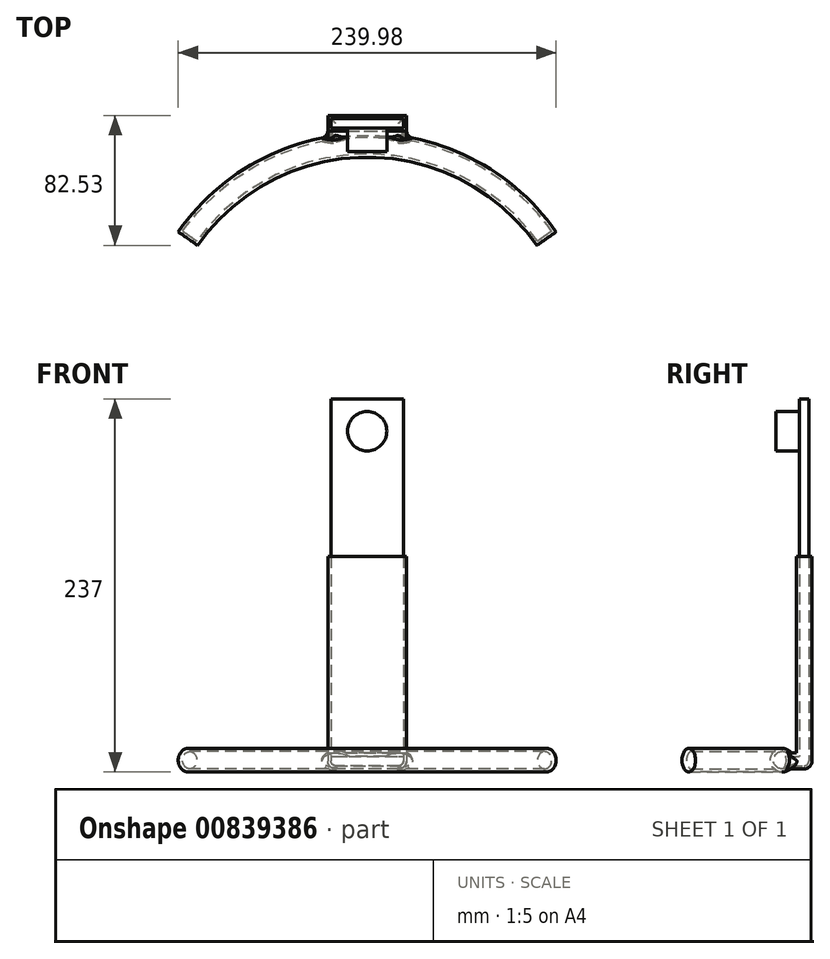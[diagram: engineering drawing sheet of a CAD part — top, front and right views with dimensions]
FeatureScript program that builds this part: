
annotation { "Feature Type Name" : "Feature", "Feature Type Description" : "" }
export const myFeature = defineFeature(function(context is Context, id is Id, definition is map)
    precondition{}
    {
        {
            var Q0;
            Q0=qCreatedBy(makeId("Right.planeOp"),FACE);
            var sketch = newSketch(context, id + "F0", { "sketchPlane" : qUnion([Q0])});
            skLineSegment(sketch, "E0", {"start": v(-100.7, 15.32) * mm, "end": v(-100.7, -57.91) * mm});
            skCircle(sketch, "E1", {"center": v(38.3, 0) * mm, "radius": 7.5 * mm});
            skSolve(sketch);
        }
        {
            var Q0;
            Q0=makeQuery(id+"F0.imprint","IMPRINT",FACE,{"disambiguationData":[TD([[makeQuery(id+"F0.imprint","IMPRINT",EDGE,{"derivedFrom":sQuery(id+"F0.wireOp",EDGE,"E1")}),1.0]])]});
            var Q1;
            Q1=sQuery(id+"F0.wireOp",EDGE,"E0");
            revolve(context, id + "F1", {"surfaceOperationType" : NewSurfaceOperationType.NEW, "entities" : qUnion([Q0]), "axis" : qUnion([Q1]), "revolveType" : RevolveType.SYMMETRIC, "angle" : 110 * degree});
        }
        {
            var Q0;
            Q0=qCreatedBy(makeId("Right.planeOp"),FACE);
            var sketch = newSketch(context, id + "F2", { "sketchPlane" : qUnion([Q0])});
            skLineSegment(sketch, "E2.bottom", {"start": v(37.26, 4.5) * mm, "end": v(57.26, 4.5) * mm});
            skLineSegment(sketch, "E2.top", {"start": v(37.26, -5.5) * mm, "end": v(57.26, -5.5) * mm});
            skLineSegment(sketch, "E2.left", {"start": v(37.26, 4.5) * mm, "end": v(37.26, -5.5) * mm});
            skLineSegment(sketch, "E2.right", {"start": v(57.26, 4.5) * mm, "end": v(57.26, -5.5) * mm});
            skSolve(sketch);
        }
        {
            var Q0;
            Q0=makeQuery(id+"F2.imprint","IMPRINT",FACE,{"disambiguationData":[TD([[makeQuery(id+"F2.imprint","IMPRINT",EDGE,{"derivedFrom":sQuery(id+"F2.wireOp",EDGE,"E2.bottom")}),-1.0]])]});
            extrude(context, id + "F3", {"entities" : qUnion([Q0]), "operationType" : NewBodyOperationType.ADD, "depth" : 25 * mm, "offsetDistance" : 25 * mm, "hasSecondDirection" : true, "secondDirectionOppositeDirection" : true, "secondDirectionDepth" : 25 * mm});
        }
        {
            var Q0;
            Q0=makeQuery(id+"F3.opExtrude","SWEPT_FACE",FACE,{"disambiguationData":[OSD([sQuery(id+"F2.wireOp",EDGE,"E2.bottom")])]});
            var sketch = newSketch(context, id + "F4", { "sketchPlane" : qUnion([Q0])});
            skLineSegment(sketch, "E3.bottom", {"start": v(-25, 47.26) * mm, "end": v(25, 47.26) * mm});
            skLineSegment(sketch, "E3.top", {"start": v(-25, 57.26) * mm, "end": v(25, 57.26) * mm});
            skLineSegment(sketch, "E3.left", {"start": v(-25, 47.26) * mm, "end": v(-25, 57.26) * mm});
            skLineSegment(sketch, "E3.right", {"start": v(25, 47.26) * mm, "end": v(25, 57.26) * mm});
            skSolve(sketch);
        }
        {
            var Q0;
            Q0=makeQuery(id+"F4.imprint","IMPRINT",FACE,{"disambiguationData":[TD([[makeQuery(id+"F4.imprint","IMPRINT",EDGE,{"derivedFrom":sQuery(id+"F4.wireOp",EDGE,"E3.bottom")}),1.0]])]});
            extrude(context, id + "F5", {"entities" : qUnion([Q0]), "operationType" : NewBodyOperationType.ADD, "depth" : 125 * mm, "offsetDistance" : 25 * mm});
        }
        {
            var Q0;
            Q0=makeQuery(id+"F3.opExtrude","SWEPT_FACE",FACE,{"disambiguationData":[OSD([sQuery(id+"F2.wireOp",EDGE,"E2.top")])]});
            fillet(context, id + "F6", {"entities" : qUnion([Q0]), "radius" : 5 * mm, "tangentPropagation" : true, "allowEdgeOverflow" : false});
        }
        {
            var Q0;
            Q0=makeQuery(id+"F5.opExtrude","CAP_FACE",FACE,{"disambiguationData":[OSD([sQuery(id+"F4.wireOp",EDGE,"E3.bottom"),sQuery(id+"F4.wireOp",EDGE,"E3.top"),sQuery(id+"F4.wireOp",EDGE,"E3.left"),sQuery(id+"F4.wireOp",EDGE,"E3.right")])],"isStart":false});
            shell(context, id + "F7", {"entities" : qUnion([Q0]), "thickness" : 2 * mm});
        }
        {
            var Q0;
            Q0=makeQuery(id+"F5.opExtrude","CAP_FACE",FACE,{"disambiguationData":[OSD([sQuery(id+"F4.wireOp",EDGE,"E3.bottom"),sQuery(id+"F4.wireOp",EDGE,"E3.top"),sQuery(id+"F4.wireOp",EDGE,"E3.left"),sQuery(id+"F4.wireOp",EDGE,"E3.right")])],"isStart":false});
            var sketch = newSketch(context, id + "F8", { "sketchPlane" : qUnion([Q0])});
            skLineSegment(sketch, "E4.bottom", {"start": v(-23, 49.26) * mm, "end": v(23, 49.26) * mm});
            skLineSegment(sketch, "E4.top", {"start": v(-23, 55.26) * mm, "end": v(23, 55.26) * mm});
            skLineSegment(sketch, "E4.left", {"start": v(-23, 49.26) * mm, "end": v(-23, 55.26) * mm});
            skLineSegment(sketch, "E4.right", {"start": v(23, 49.26) * mm, "end": v(23, 55.26) * mm});
            skSolve(sketch);
        }
        {
            var Q0;
            Q0 = qSketchRegion(id + "F8", true);
            extrude(context, id + "F9", {"entities" : qUnion([Q0]), "depth" : 100 * mm, "offsetDistance" : 25 * mm});
        }
        {
            var Q0;
            Q0=makeQuery(id+"F9.opExtrude","SWEPT_FACE",FACE,{"disambiguationData":[OSD([sQuery(id+"F8.wireOp",EDGE,"E4.bottom")])]});
            var sketch = newSketch(context, id + "F10", { "sketchPlane" : qUnion([Q0])});
            skCircle(sketch, "E5", {"center": v(0, 209) * mm, "radius": 12.5 * mm});
            skSolve(sketch);
        }
        {
            var Q0;
            Q0=makeQuery(id+"F10.imprint","IMPRINT",FACE,{"disambiguationData":[TD([[makeQuery(id+"F10.imprint","IMPRINT",EDGE,{"derivedFrom":sQuery(id+"F10.wireOp",EDGE,"E5")}),1.0]])]});
            extrude(context, id + "F11", {"entities" : qUnion([Q0]), "operationType" : NewBodyOperationType.ADD, "depth" : 15 * mm, "offsetDistance" : 25 * mm});
        }
    });
